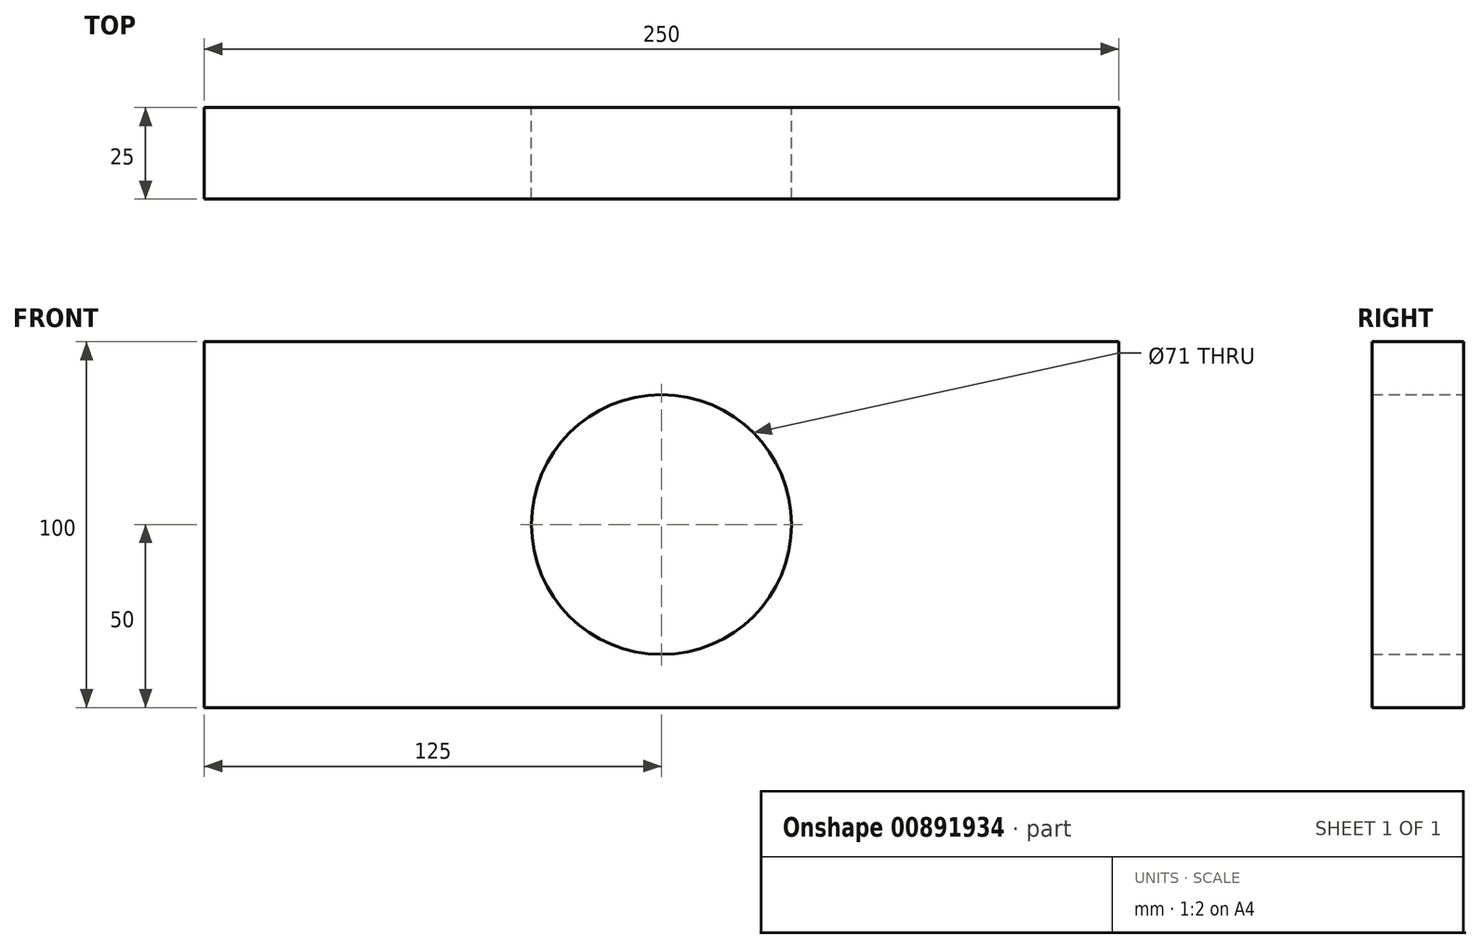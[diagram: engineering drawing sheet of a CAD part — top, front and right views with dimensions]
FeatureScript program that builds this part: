
annotation { "Feature Type Name" : "Feature", "Feature Type Description" : "" }
export const myFeature = defineFeature(function(context is Context, id is Id, definition is map)
    precondition{}
    {
        {
            var Q0;
            Q0=qCreatedBy(makeId("Front.planeOp"),FACE);
            var sketch = newSketch(context, id + "F0", { "sketchPlane" : qUnion([Q0])});
            skLineSegment(sketch, "E0.bottom", {"start": v(125, 50) * mm, "end": v(-125, 50) * mm});
            skLineSegment(sketch, "E0.top", {"start": v(125, -50) * mm, "end": v(-125, -50) * mm});
            skLineSegment(sketch, "E0.left", {"start": v(125, 50) * mm, "end": v(125, -50) * mm});
            skLineSegment(sketch, "E0.right", {"start": v(-125, 50) * mm, "end": v(-125, -50) * mm});
            skPoint(sketch, "E0.middle", {"position": v(0, 0) * mm});
            skCircle(sketch, "E1", {"center": v(0, 0) * mm, "radius": 35.5 * mm});
            skSolve(sketch);
        }
        {
            var Q0;
            Q0 = qSketchRegion(id + "F0", true);
            extrude(context, id + "F1", {"entities" : qUnion([Q0]), "depth" : 25 * mm, "offsetDistance" : 25 * mm});
        }
    });
